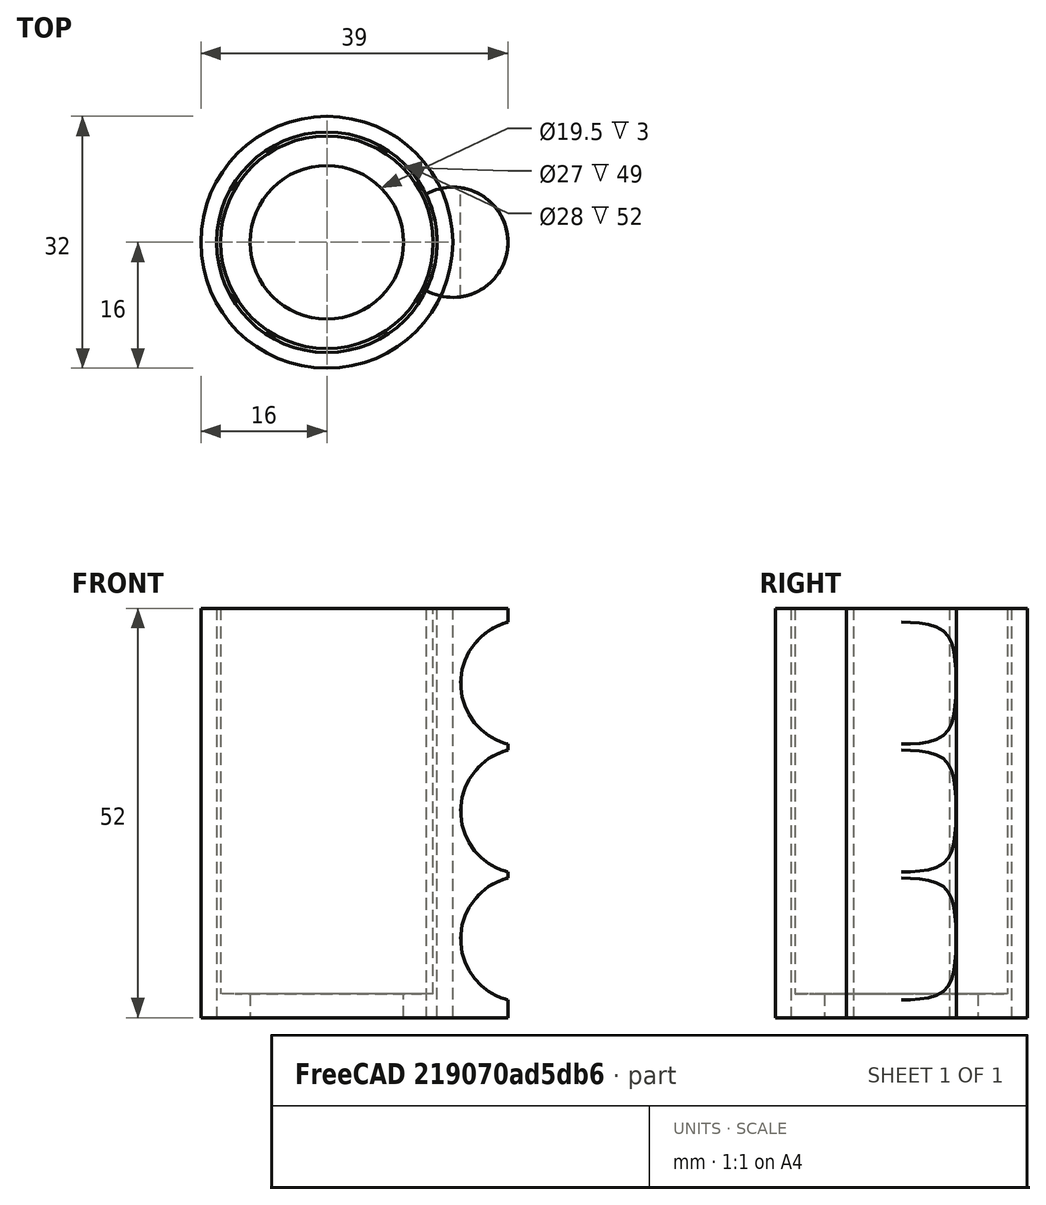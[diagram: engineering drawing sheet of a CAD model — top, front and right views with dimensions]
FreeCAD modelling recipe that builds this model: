
FCSTD DOCUMENT  (FreeCAD 1.0R39109 (Git))
Label: Thelio-Fidget-Toy
License: All rights reserved
LicenseURL: https://en.wikipedia.org/wiki/All_rights_reserved
objects: Part::Cylinder×11, Part::Cut×8
note: 19 computed .brp shape members not serialized (recipe doc carries the construction recipe); baked Part::Feature solids carry a one-line shape summary decoded from their .brp

FEATURE [Part::Cylinder] Cylinder  label="Power Button"
  Angle = 360
  AttacherType = Attacher::AttachEngine3D
  FirstAngle = 0
  Height = 52
  Radius = 9.75
  SecondAngle = 0
FEATURE [Part::Cylinder] Cylinder006
  Angle = 360
  AttacherType = Attacher::AttachEngine3D
  FirstAngle = 0
  Height = 52
  Radius = 14
  SecondAngle = 0
FEATURE [Part::Cylinder] Cylinder002
  Angle = 360
  AttacherType = Attacher::AttachEngine3D
  FirstAngle = 0
  Height = 52
  Radius = 14
  SecondAngle = 0
FEATURE [Part::Cylinder] Cylinder001
  Angle = 360
  AttacherType = Attacher::AttachEngine3D
  FirstAngle = 0
  Height = 49
  Placement = pos=(0,0,3) rot=(0,0,1;0rad)
  Radius = 12
  SecondAngle = 0
FEATURE [Part::Cut] Cut
  Base = -> Cylinder002
  Tool = -> Cylinder001
FEATURE [Part::Cut] Cut001
  Base = -> Cut
  Tool = -> Cylinder
FEATURE [Part::Cylinder] Cylinder007  label="Cylinder"
  Angle = 360
  AttacherType = Attacher::AttachEngine3D
  FirstAngle = 0
  Height = 49
  Placement = pos=(0,0,3) rot=(0,0,1;0rad)
  Radius = 13.5
  SecondAngle = 0
FEATURE [Part::Cut] Cut002
  Base = -> Cut001
  Tool = -> Cylinder007
FEATURE [Part::Cylinder] Cylinder008
  Angle = 360
  AttacherType = Attacher::AttachEngine3D
  FirstAngle = 0
  Height = 52
  Radius = 16
  SecondAngle = 0
FEATURE [Part::Cut] Cut003
  Base = -> Cylinder008
  Tool = -> Cylinder006
FEATURE [Part::Cylinder] Cylinder009
  Angle = 360
  AttacherType = Attacher::AttachEngine3D
  FirstAngle = 0
  Height = 52
  Placement = pos=(16,0,0) rot=(0,0,1;0rad)
  Radius = 7
  SecondAngle = 0
FEATURE [Part::Cylinder] Cylinder010
  Angle = 360
  AttacherType = Attacher::AttachEngine3D
  FirstAngle = 0
  Height = 52
  Radius = 14
  SecondAngle = 0
FEATURE [Part::Cut] Cut004
  Base = -> Cylinder009
  Tool = -> Cylinder010
FEATURE [Part::Cylinder] Cylinder011
  Angle = 360
  AttacherType = Attacher::AttachEngine3D
  FirstAngle = 0
  Height = 14
  Placement = pos=(25,7,10) rot=(1,0,0;1.5708rad)
  Radius = 8
  SecondAngle = 0
FEATURE [Part::Cylinder] Cylinder012
  Angle = 360
  AttacherType = Attacher::AttachEngine3D
  FirstAngle = 0
  Height = 14
  Placement = pos=(25,7,26.25) rot=(1,0,0;1.5708rad)
  Radius = 8
  SecondAngle = 0
FEATURE [Part::Cylinder] Cylinder013
  Angle = 360
  AttacherType = Attacher::AttachEngine3D
  FirstAngle = 0
  Height = 14
  Placement = pos=(25,7,42.5) rot=(1,0,0;1.5708rad)
  Radius = 8
  SecondAngle = 0
FEATURE [Part::Cut] Cut005
  Base = -> Cut004
  Tool = -> Cylinder011
FEATURE [Part::Cut] Cut006
  Base = -> Cut005
  Tool = -> Cylinder012
FEATURE [Part::Cut] Cut007
  Base = -> Cut006
  Tool = -> Cylinder013
